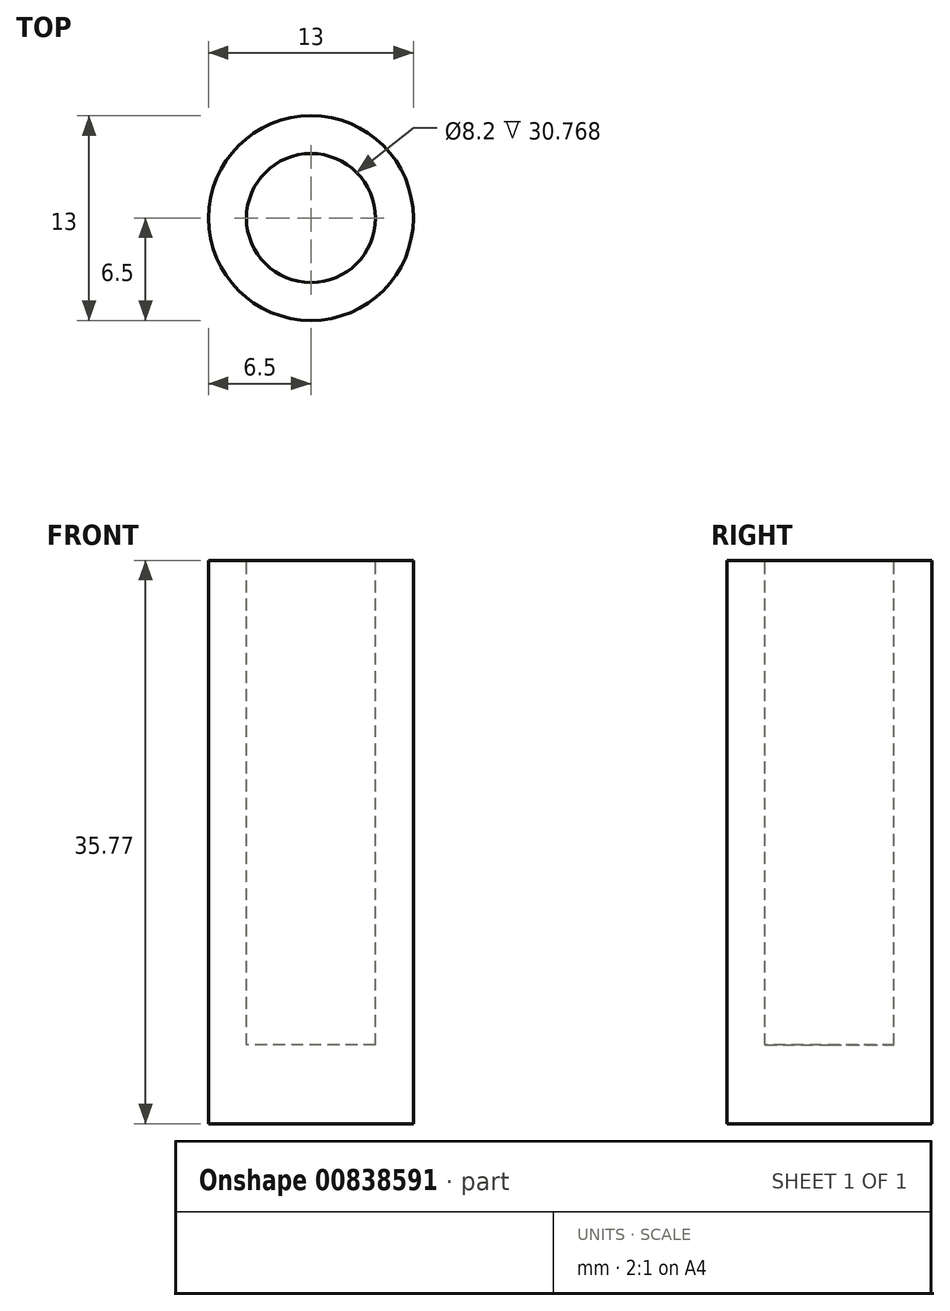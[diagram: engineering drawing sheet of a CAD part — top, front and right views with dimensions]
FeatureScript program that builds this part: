
annotation { "Feature Type Name" : "Feature", "Feature Type Description" : "" }
export const myFeature = defineFeature(function(context is Context, id is Id, definition is map)
    precondition{}
    {
        {
            var Q0;
            Q0=qCreatedBy(makeId("Front.planeOp"),FACE);
            var sketch = newSketch(context, id + "F0", { "sketchPlane" : qUnion([Q0])});
            skLineSegment(sketch, "E0", {"start": v(0, 35.9) * mm, "end": v(0, 0) * mm, "construction": true});
            skLineSegment(sketch, "E1", {"start": v(4.1, 0) * mm, "end": v(4.1, 35.77) * mm});
            skLineSegment(sketch, "E2", {"start": v(6.5, 0) * mm, "end": v(6.5, 35.77) * mm});
            skLineSegment(sketch, "E3", {"start": v(13.82, 5) * mm, "end": v(13.82, 0) * mm});
            skLineSegment(sketch, "E4", {"start": v(13.82, 0) * mm, "end": v(13.82, 5) * mm});
            skLineSegment(sketch, "E5", {"start": v(0, 0) * mm, "end": v(13.82, 0) * mm});
            skLineSegment(sketch, "E6", {"start": v(13.82, 5) * mm, "end": v(0, 5) * mm});
            skLineSegment(sketch, "E7", {"start": v(4.1, 35.77) * mm, "end": v(6.5, 35.77) * mm});
            skLineSegment(sketch, "E8", {"start": v(0, 5) * mm, "end": v(0, 0) * mm});
            skSolve(sketch);
        }
        {
            var Q0;
            {var subQ0=sQuery(id+"F0.wireOp",EDGE,"E7");Q0=makeQuery(id+"F0.imprint","IMPRINT",FACE,{"disambiguationData":[TD([[makeQuery(id+"F0.imprint","IMPRINT",EDGE,{"derivedFrom":subQ0}),-1.0]])]});}
            var Q1;
            Q1=sQuery(id+"F0.wireOp",EDGE,"E0");
            revolve(context, id + "F1", {"surfaceOperationType" : NewSurfaceOperationType.NEW, "entities" : qUnion([Q0]), "axis" : qUnion([Q1]), "revolveType" : RevolveType.FULL});
        }
        {
            var Q0;
            {var subQ5=sQuery(id+"F0.wireOp",EDGE,"E8");Q0=makeQuery(id+"F0.imprint","IMPRINT",FACE,{"disambiguationData":[TD([[makeQuery(id+"F0.imprint","IMPRINT",EDGE,{"derivedFrom":subQ5}),1.0]])]});}
            var Q1;
            {var subQ0=sQuery(id+"F0.wireOp",EDGE,"E5");var subQ1=sQuery(id+"F0.wireOp",EDGE,"E1");var subQ2=makeQuery(id+"F0.imprint","INTERSECT",VERTEX,{"derivedFrom":[subQ1,subQ0]});Q1=makeQuery(id+"F0.imprint","IMPRINT",FACE,{"disambiguationData":[TD([[makeQuery(id+"F0.imprint","IMPRINT",EDGE,{"disambiguationData":[TD([[subQ2,-1.0]])],"derivedFrom":subQ1}),-1.0]])]});}
            var Q2;
            {var subQ5=sQuery(id+"F0.wireOp",EDGE,"E4");Q2=makeQuery(id+"F0.imprint","IMPRINT",FACE,{"disambiguationData":[TD([[makeQuery(id+"F0.imprint","IMPRINT",EDGE,{"derivedFrom":subQ5}),1.0]])]});}
            var Q3;
            Q3=sQuery(id+"F0.wireOp",EDGE,"E8");
            revolve(context, id + "F2", {"operationType" : NewBodyOperationType.ADD, "surfaceOperationType" : NewSurfaceOperationType.NEW, "entities" : qUnion([Q0, Q1, Q2]), "axis" : qUnion([Q3]), "revolveType" : RevolveType.FULL});
        }
    });
